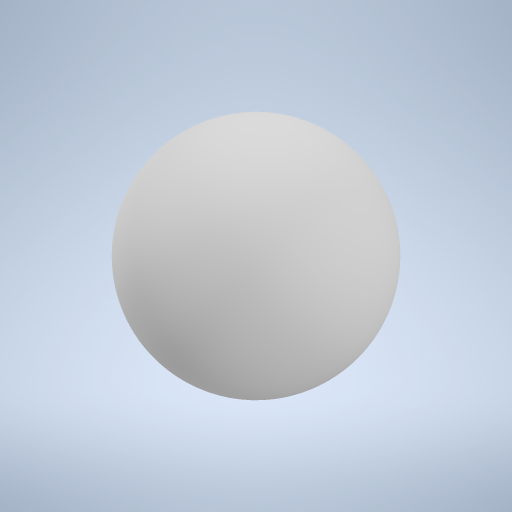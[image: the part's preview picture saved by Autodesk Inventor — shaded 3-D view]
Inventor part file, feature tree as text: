
AUTODESK INVENTOR PART (.ipt)
format: ipt  version: 2024 (Build 280153000, 153)  size: 244,224 bytes
history: native  units: in
note: dims shown in document units (in); Inventor stores cm internally (conversion verified against a paired STEP export)
features: revolve x1, sketch x1
ambient origin geometry x8: Origin, YZ Plane, XZ Plane, XY Plane, X Axis, Y Axis, Z Axis, Center Point
bodies: Solid1 (feature_tree)
feature tree (2):
  revolve  "Revolution1"  [1 undecoded]
  sketch  "Sketch1"  dims[d0=19.685in d1=19.685in d2=360.0deg]
note: 1 required parameter value undecoded (feature->parameter linkage not recoverable at this tier; creation-order binding heuristic only, values carry confidence <= 0.55)
